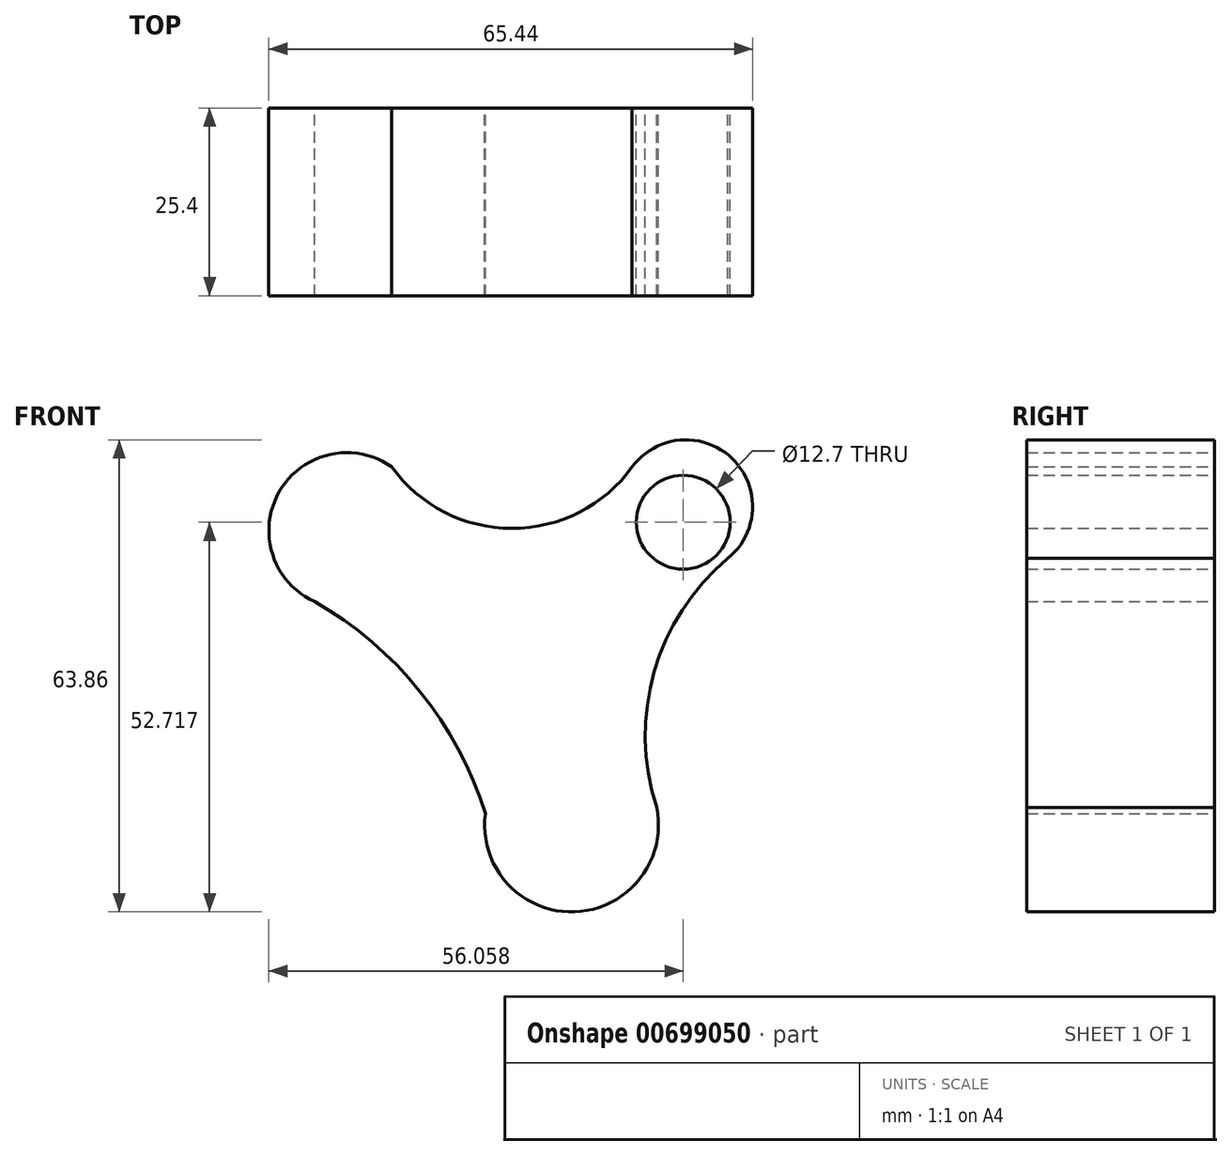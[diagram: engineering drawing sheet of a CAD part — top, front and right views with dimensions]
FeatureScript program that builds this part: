
annotation { "Feature Type Name" : "Feature", "Feature Type Description" : "" }
export const myFeature = defineFeature(function(context is Context, id is Id, definition is map)
    precondition{}
    {
        {
            var Q0;
            Q0=qCreatedBy(makeId("Front.planeOp"),FACE);
            var sketch = newSketch(context, id + "F0", { "sketchPlane" : qUnion([Q0])});
            skArc(sketch, "E0", {"start": v(-35.83, 57.13) * mm, "mid": v(-51.06, 53.76) * mm, "end": v(-46.29, 38.9) * mm});
            skArc(sketch, "E1", {"start": v(-35.83, 57.13) * mm, "mid": v(-19.57, 48.8) * mm, "end": v(-3.3, 57.13) * mm});
            skArc(sketch, "E2", {"start": v(9.64, 44.75) * mm, "mid": v(10.19, 58.3) * mm, "end": v(-3.3, 57.13) * mm});
            skArc(sketch, "E3", {"start": v(-23.17, 10.22) * mm, "mid": v(-32, 26.75) * mm, "end": v(-46.29, 38.9) * mm});
            skArc(sketch, "E4", {"start": v(9.64, 44.75) * mm, "mid": v(-0.34, 29.4) * mm, "end": v(0, 11.08) * mm});
            skArc(sketch, "E5", {"start": v(-23.17, 10.22) * mm, "mid": v(-11.07, -3.06) * mm, "end": v(0, 11.08) * mm});
            skSolve(sketch);
        }
        {
            var Q0;
            Q0=qCreatedBy(makeId("Front.planeOp"),FACE);
            var sketch = newSketch(context, id + "F1", { "sketchPlane" : qUnion([Q0])});
            skCircle(sketch, "E6", {"center": v(-41.88, 48.5) * mm, "radius": 6.35 * mm});
            skCircle(sketch, "E7", {"center": v(3.6, 49.65) * mm, "radius": 6.35 * mm});
            skCircle(sketch, "E8", {"center": v(-11.94, 6.76) * mm, "radius": 6.35 * mm});
            skCircle(sketch, "E9", {"center": v(-15.1, 28.35) * mm, "radius": 6.35 * mm});
            skSolve(sketch);
        }
        {
            var Q0;
            Q0=makeQuery(id+"F0.imprint","IMPRINT",FACE,{"disambiguationData":[TD([[makeQuery(id+"F0.imprint","IMPRINT",EDGE,{"derivedFrom":sQuery(id+"F0.wireOp",EDGE,"E0")}),1.0]])]});
            extrude(context, id + "F2", {"entities" : qUnion([Q0]), "depth" : 25.4 * mm, "offsetDistance" : 25.4 * mm});
        }
        {
            var Q0;
            Q0=makeQuery(id+"F1.imprint","IMPRINT",FACE,{"disambiguationData":[TD([[makeQuery(id+"F1.imprint","IMPRINT",EDGE,{"derivedFrom":sQuery(id+"F1.wireOp",EDGE,"E7")}),1.0]])]});
            extrude(context, id + "F3", {"entities" : qUnion([Q0]), "operationType" : NewBodyOperationType.REMOVE, "depth" : 25.4 * mm, "offsetDistance" : 25.4 * mm});
        }
        {
            var Q0;
            Q0=makeQuery(id+"F1.imprint","IMPRINT",FACE,{"disambiguationData":[TD([[makeQuery(id+"F1.imprint","IMPRINT",EDGE,{"derivedFrom":sQuery(id+"F1.wireOp",EDGE,"E6")}),1.0]])]});
            var Q1;
            Q1=sQuery(id+"F1.wireOp",EDGE,"E6");
            extrude(context, id + "F4", {"entities" : qUnion([Q0]), "operationType" : NewBodyOperationType.REMOVE, "surfaceEntities" : qUnion([Q1]), "oppositeDirection" : true, "depth" : 25.4 * mm, "offsetDistance" : 25.4 * mm});
        }
    });
